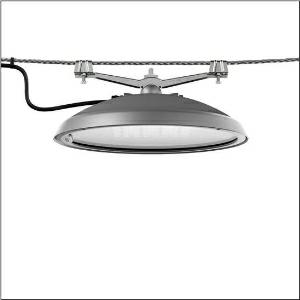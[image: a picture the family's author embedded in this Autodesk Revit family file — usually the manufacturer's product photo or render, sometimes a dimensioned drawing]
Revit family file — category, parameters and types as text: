
# Revit family: dl_r__50_iq_mini___st1_0s_5xa248w41f08ge_d0d2
name_source: partatom
category: Lighting Fixtures
units: mm (PartAtom-declared; Revit-internal decimal feet)

## family parameters
Cut with Voids When Loaded = No
Host = Face
Light Source = No
Part Type = Normal
Room Calculation Point = No
Round Connector Dimension = Use Diameter
Shared = No

## types (1)
- --- (1 x LED, 5190 lm, 31.2 W, 4000K)
    Apparent Load = 31 VA
    CIE Flux Codes = 37 72 97 100 100
    Color Rendering = 70
    Color Temperature = 4000K
    Default Elevation = 1800 mm
    Description = DL® 50 iQ mini, catenary luminaire, primary light control with lens, of PMMA, primary optical cover: cover, of toughened safety glass, transparent, light distribution: ST1.0s, light emission: direct distribution, primary light characteristic: symmetric, installation type: suspended mounting, LED, High Power LED, rated luminous flux: 5.190lm, luminous efficacy: 166lm/W, light colour: 740, colour temperature: 4000K, control gear: iQ Street-Remote, control: optimised constant luminous flux control (CLO 2.0), Desk-Remote (wireless, voltage-free reading and setting of iQ features in the workshop via application-optimized NFC function/RFID function), Light-Fading, Smart-Wire, Night-Set, Lumen-Switch, Temp-Guard, Auto-Match, Street-Remote, mains connection: 230..240V, AC, 50/60Hz, start of lifetime: 31W, end of service life: 32W, reduction: 15W, luminaire housing, of diecast aluminium, powder-coated, Siteco® metallic grey (DB 702S), diameter: 500mm, height: 115mm, mounting height: 4..12m, protection rating (complete): IP66, insulation class (complete): insulation class II (safety insulation), certification: CE, ENEC, ENEC+, VDE, impact resistance: IK08, permissible operating ambient temperature for outdoor applications: -25..+40°C, standard-compliant lighting for roads and squares, packaging unit: 1 piece

Light Distribution: ST1.0s
    Height = 124 mm  [stored 0.406824 ft]
    Lamp = 1 x LED
    Lamp Light Flux = 5190 lm
    Lamp Power = 31.2 W
    Lamp count = 1
    Length = 500 mm
    Luminous efficacy = 166 lm/W
    Manufacturer = Siteco
    ModVariant = No
    Model = 5XA248W41F08GE
    Number of Poles = 1
    OnlyDefault = Yes
    Power Factor = 1
    Product Name = DL® 50 iQ mini | ST1.0s
    Product group = catenary luminaire
    ProductGroupID = 6300
    Protection Class = Protection class II
    Protection Degree = IP 66
    RLX_Detail_Level = 1
    RLX_Emergency_Light_Flux = 0 lm
    RLX_Emergency_Type = 0
    RLX_Emergency_Type_DB = No
    RlxData = <blob elided: 123437 chars, md5=8ffa39ed>
    Socket = socket
    Standby Power = 0 W
    System Light Flux = 5190 lm
    System Power = 31 W
    Type Comments = factory setting: luminous flux: 100 % | dim-lin: 254 | 325 mA
    Type Image = l_1242791.jpg
    URL = http://relux.com
    VarID = @adj_162309
    Voltage = 0 V
    Weight = 0.00 kg
    Width = 0 mm  [stored 0 ft]

note: [stored X ft] marks values corroborated as IEEE doubles in the binary element streams (Revit-internal decimal feet)

## geometry (parser evidence)
native form markers: Blend x4, Sweep x14
no freeform markers — native parametric forms only
